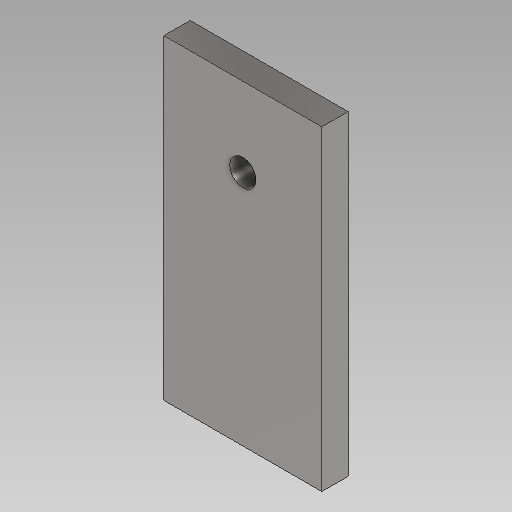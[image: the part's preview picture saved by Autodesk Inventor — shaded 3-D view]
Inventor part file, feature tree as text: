
AUTODESK INVENTOR PART (.ipt)
format: ipt  version: 2021 (Build 250183000, 183)  size: 118,272 bytes
history: native  units: mm
features: sketch x2, hole x1
ambient origin geometry x8: Origin, YZ Plane, XZ Plane, XY Plane, X Axis, Y Axis, Z Axis, Center Point
bodies: Solid1 (feature_tree)
feature tree (3):
  hole  "Hole1"  [1 undecoded]
  sketch  "Sketch1"  dims[d0=30.0mm d1=15.0mm]
  sketch  "Sketch2"  dims[d2=60.0mm d3=30.0mm d4=5.0mm d5=0.0mm d6=45.0mm d7=5.0mm d8=6.0mm d9=4.0mm d10=2.0mm d11=90.0deg d12=8.0mm d13=20.594885mm]
note: 1 required parameter value undecoded (feature->parameter linkage not recoverable at this tier; creation-order binding heuristic only, values carry confidence <= 0.55)
